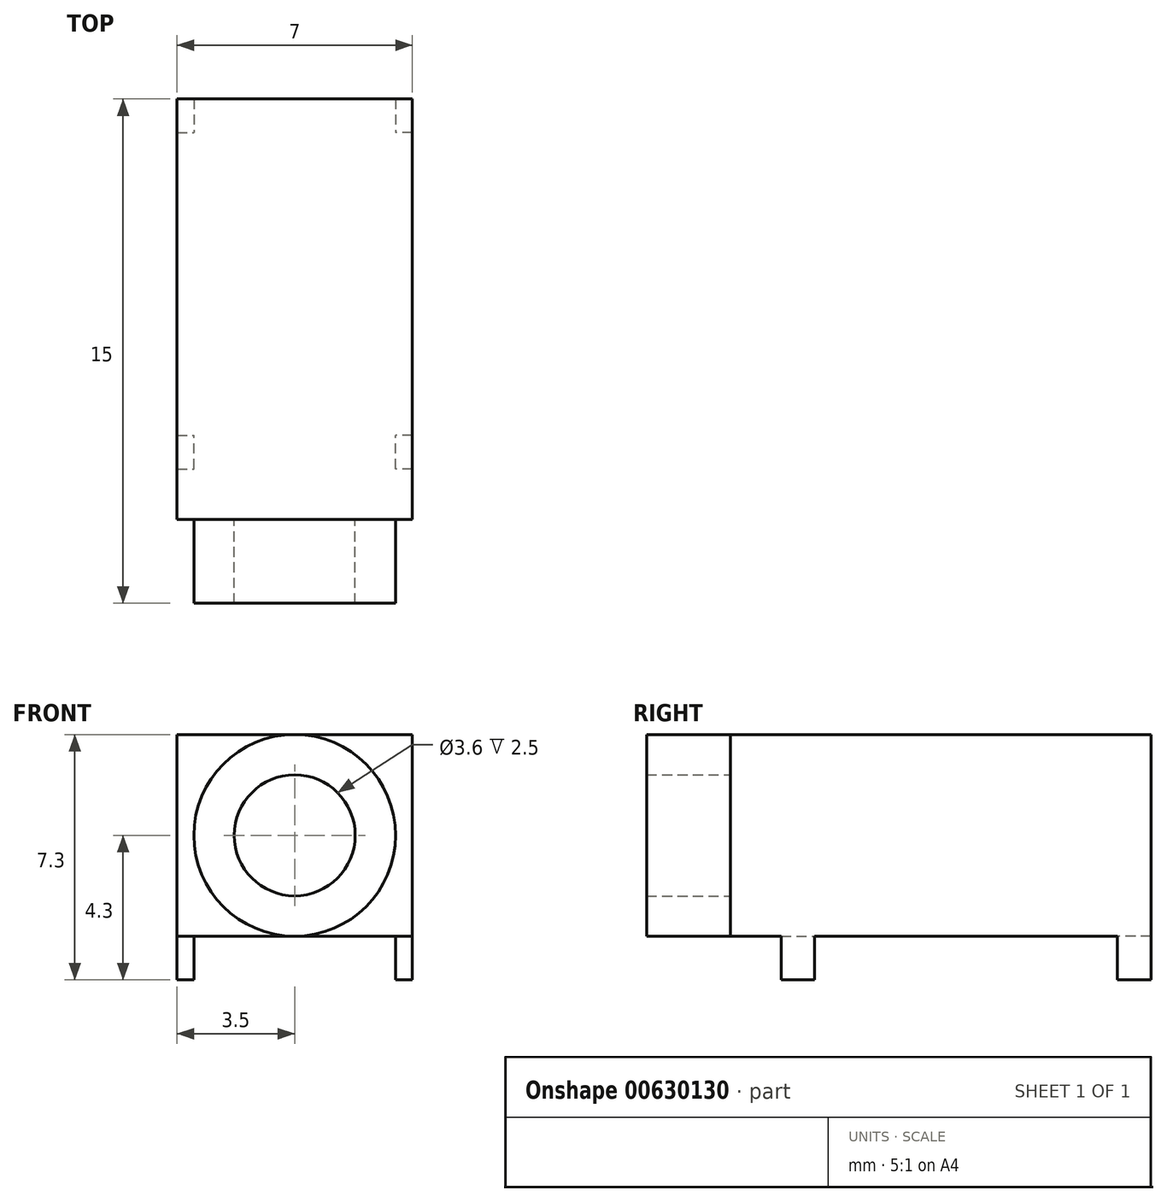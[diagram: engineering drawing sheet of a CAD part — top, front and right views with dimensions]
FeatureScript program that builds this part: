
annotation { "Feature Type Name" : "Feature", "Feature Type Description" : "" }
export const myFeature = defineFeature(function(context is Context, id is Id, definition is map)
    precondition{}
    {
        {
            var Q0;
            Q0=qCreatedBy(makeId("Front.planeOp"),FACE);
            var sketch = newSketch(context, id + "F0", { "sketchPlane" : qUnion([Q0])});
            skLineSegment(sketch, "E0.bottom", {"start": v(0, 0) * mm, "end": v(7, 0) * mm});
            skLineSegment(sketch, "E0.top", {"start": v(0, 6) * mm, "end": v(7, 6) * mm});
            skLineSegment(sketch, "E0.left", {"start": v(0, 0) * mm, "end": v(0, 6) * mm});
            skLineSegment(sketch, "E0.right", {"start": v(7, 0) * mm, "end": v(7, 6) * mm});
            skSolve(sketch);
        }
        {
            var Q0;
            Q0=qSketchRegion(id+"F0",true);
            extrude(context, id + "F1", {"entities" : qUnion([Q0]), "depth" : 12.5 * mm});
        }
        {
            var Q0;
            Q0=makeQuery(id+"F1.opExtrude","CAP_FACE",FACE,{"disambiguationData":[OSD([sQuery(id+"F0.wireOp",EDGE,"E0.bottom"),sQuery(id+"F0.wireOp",EDGE,"E0.top"),sQuery(id+"F0.wireOp",EDGE,"E0.left"),sQuery(id+"F0.wireOp",EDGE,"E0.right")])],"isStart":false});
            var sketch = newSketch(context, id + "F2", { "sketchPlane" : qUnion([Q0])});
            skCircle(sketch, "E1", {"center": v(3.5, 3) * mm, "radius": 3 * mm});
            skLineSegment(sketch, "E2", {"start": v(3.5, 0) * mm, "end": v(3.5, 6) * mm, "construction": true});
            skCircle(sketch, "E3", {"center": v(3.5, 3) * mm, "radius": 1.8 * mm});
            skSolve(sketch);
        }
        {
            var Q0;
            Q0=qSketchRegion(id+"F2",true);
            extrude(context, id + "F3", {"entities" : qUnion([Q0]), "operationType" : NewBodyOperationType.ADD, "depth" : 2.5 * mm});
        }
        {
            var Q0;
            Q0=makeQuery(id+"F1.opExtrude","SWEPT_FACE",FACE,{"disambiguationData":[OSD([sQuery(id+"F0.wireOp",EDGE,"E0.bottom")])]});
            var sketch = newSketch(context, id + "F4", { "sketchPlane" : qUnion([Q0])});
            skLineSegment(sketch, "E4", {"start": v(3.5, 12.5) * mm, "end": v(3.5, 0) * mm, "construction": true});
            skLineSegment(sketch, "E5.bottom", {"start": v(0, 0) * mm, "end": v(0.5, 0) * mm});
            skLineSegment(sketch, "E5.top", {"start": v(0, 1) * mm, "end": v(0.5, 1) * mm});
            skLineSegment(sketch, "E5.left", {"start": v(0, 0) * mm, "end": v(0, 1) * mm});
            skLineSegment(sketch, "E5.right", {"start": v(0.5, 0) * mm, "end": v(0.5, 1) * mm});
            skLineSegment(sketch, "E6.bottom", {"start": v(0, 11) * mm, "end": v(0.5, 11) * mm});
            skLineSegment(sketch, "E6.top", {"start": v(0, 10) * mm, "end": v(0.5, 10) * mm});
            skLineSegment(sketch, "E6.left", {"start": v(0, 11) * mm, "end": v(0, 10) * mm});
            skLineSegment(sketch, "E6.right", {"start": v(0.5, 11) * mm, "end": v(0.5, 10) * mm});
            skLineSegment(sketch, "E7.MirrorCS", {"start": v(7, 10) * mm, "end": v(6.5, 10) * mm});
            skLineSegment(sketch, "E8.MirrorCS", {"start": v(7, 11) * mm, "end": v(6.5, 11) * mm});
            skLineSegment(sketch, "E9.MirrorCS", {"start": v(6.5, 0) * mm, "end": v(6.5, 1) * mm});
            skLineSegment(sketch, "E10.MirrorCS", {"start": v(7, 0) * mm, "end": v(7, 1) * mm});
            skLineSegment(sketch, "E11.MirrorCS", {"start": v(7, 1) * mm, "end": v(6.5, 1) * mm});
            skLineSegment(sketch, "E12.MirrorCS", {"start": v(7, 0) * mm, "end": v(6.5, 0) * mm});
            skLineSegment(sketch, "E13.MirrorCS", {"start": v(7, 11) * mm, "end": v(7, 10) * mm});
            skLineSegment(sketch, "E14.MirrorCS", {"start": v(6.5, 11) * mm, "end": v(6.5, 10) * mm});
            skSolve(sketch);
        }
        {
            var Q0;
            Q0=qSketchRegion(id+"F4",true);
            extrude(context, id + "F5", {"entities" : qUnion([Q0]), "operationType" : NewBodyOperationType.ADD, "depth" : 1.3 * mm});
        }
    });
